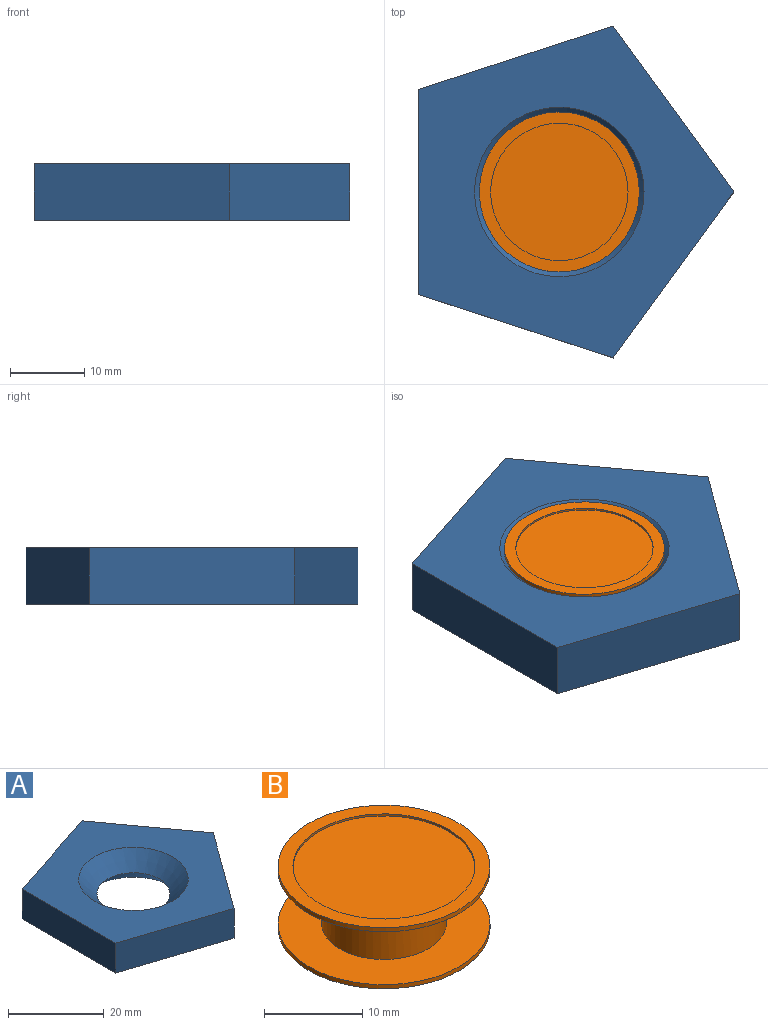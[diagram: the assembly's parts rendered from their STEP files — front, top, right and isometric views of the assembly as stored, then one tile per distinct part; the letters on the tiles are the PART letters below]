
ASSEMBLY  parts=2 mates=1
PART A: 9 faces, bbox 42.6x44.8x7.6 mm
  f0: plane 27.68x7.62mm, normal (-1,0,0), area 210.9mm2, adj f1,f4,f5,f6
  f1: plane 26.33x8.55mm, normal (-0.31,-0.95,0), area 210.9mm2, adj f0,f2,f5,f6
  f2: plane 22.39x16.27mm, normal (0.81,-0.59,0), area 210.9mm2, adj f1,f3,f5,f6
  f3: plane 22.39x16.27mm, normal (0.81,0.59,0), area 210.9mm2, adj f2,f4,f5,f6
  f4: plane 26.33x8.55mm, normal (-0.31,0.95,0), area 210.9mm2, adj f0,f3,f5,f6
  f5: plane 44.79x42.6mm, normal (0,0,1), area 907.9mm2, adj f0,f1,f2,f3,f4,f7
  f6: plane 44.79x42.6mm, normal (0,0,-1), area 907.9mm2, adj f0,f1,f2,f3,f4,f8
  f7: cone r=7.62mm half-angle=45deg, axis (0,0,1), area 322.5mm2, adj f5,f8
  f8: cone r=11.43mm half-angle=45deg, axis (0,0,-1), area 322.5mm2, adj f6,f7
PART B: 11 faces, bbox 21.6x21.6x7.6 mm
  f0: cylinder r=6.35mm len=12.7mm, axis (0,0,-1), area 263.5mm2, adj f2,f5
  f1: cylinder r=10.79mm len=21.59mm, axis (0,0,-1), area 34.5mm2, adj f2,f3
  f2: plane 21.59x21.59mm, normal (0,0,1), area 239.4mm2, adj f0,f1
  f3: plane 21.59x21.59mm, normal (0,0,-1), area 96.1mm2, adj f1,f9
  f4: cylinder r=10.79mm len=21.59mm, axis (0,0,1), area 34.5mm2, adj f5,f6
  f5: plane 21.59x21.59mm, normal (0,0,-1), area 239.4mm2, adj f0,f4
  f6: plane 21.59x21.59mm, normal (0,0,1), area 96.1mm2, adj f4,f7
  f7: cylinder r=9.27mm len=18.54mm, axis (0,0,1), area 14.8mm2, adj f6,f8
  f8: plane 18.54x18.54mm, normal (0,0,1), area 270mm2, adj f7
  f9: cylinder r=9.27mm len=18.54mm, axis (0,0,-1), area 14.8mm2, adj f3,f10
  f10: plane 18.54x18.54mm, normal (0,0,-1), area 270mm2, adj f9
PLACE A t=(-17.92,9.74,5.33)mm
PLACE B t=(-17.92,9.74,5.33)mm
MATE fastened B.f0 <-> A.f7  axis (0,0,-1) through (-17.92,9.74,9.14)mm
